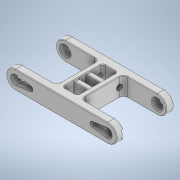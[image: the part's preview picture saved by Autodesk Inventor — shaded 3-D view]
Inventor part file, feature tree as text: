
AUTODESK INVENTOR PART (.ipt)
format: ipt  version: 2020.3 (Build 243373000, 373)  size: 555,520 bytes
history: native  units: mm
features: sketch x7, other x3
ambient origin geometry x8: Origin, YZ Plane, XZ Plane, XY Plane, X Axis, Y Axis, Z Axis, Center Point
bodies: Solid1 (feature_tree)
feature tree (10):
  other  "LegMiddle_Final_1.ipt"
  other  "Solid1::LegMiddle_Final_1.ipt"
  other  "TaggingFeature1"
  sketch  "Sketch1"  dims[d0=10.0mm]
  sketch  "Sketch2"
  sketch  "Sketch5"
  sketch  "Sketch14"
  sketch  "Sketch6"
  sketch  "Sketch12"
  sketch  "Sketch13"
